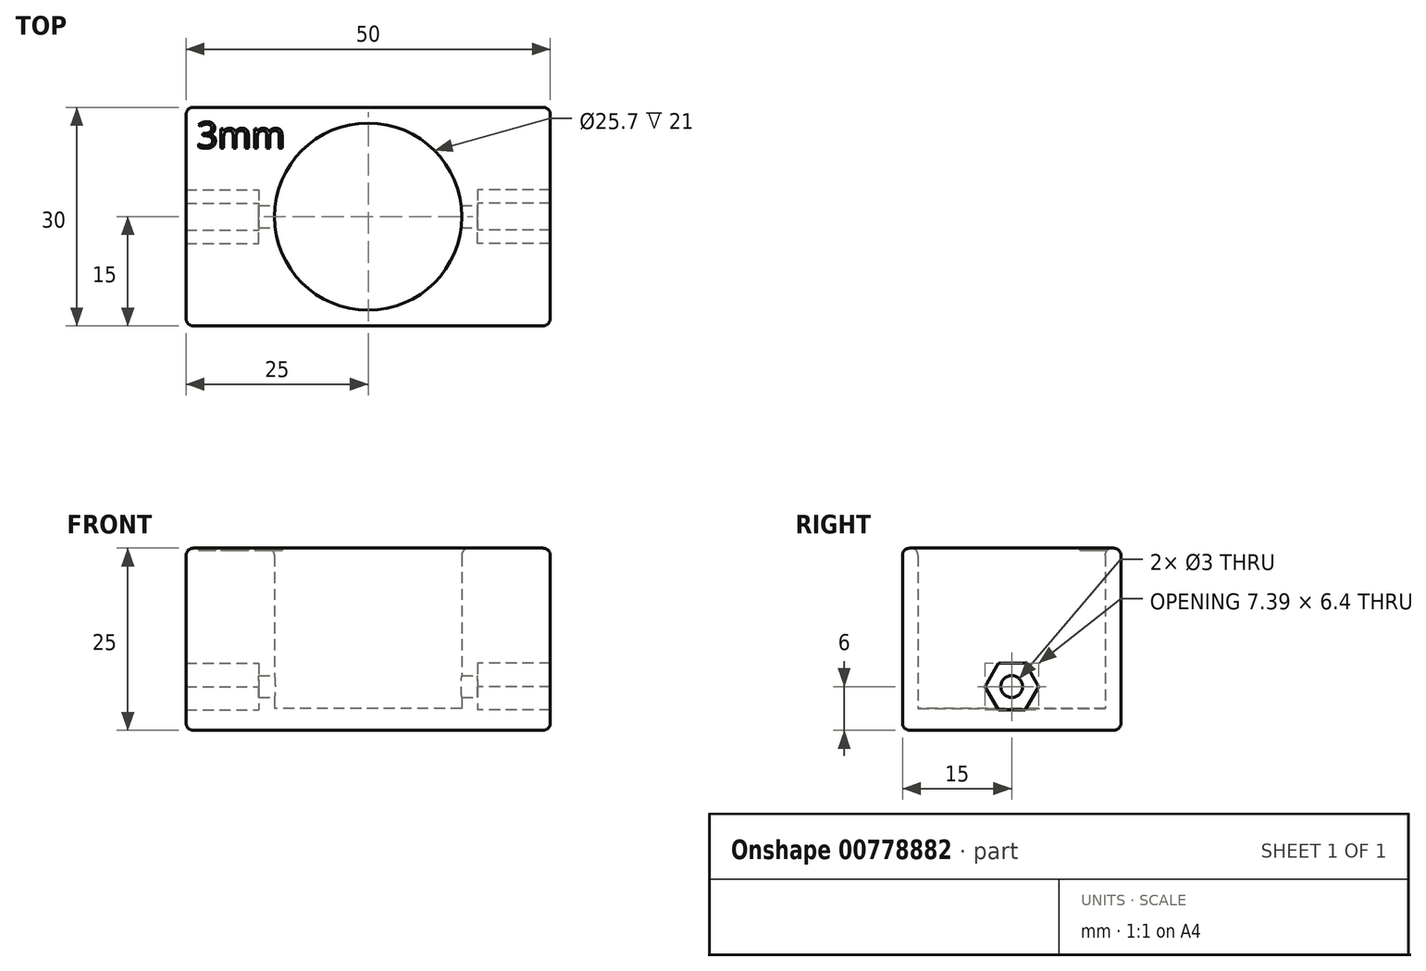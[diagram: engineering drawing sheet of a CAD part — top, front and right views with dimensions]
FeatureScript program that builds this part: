
annotation { "Feature Type Name" : "Feature", "Feature Type Description" : "" }
export const myFeature = defineFeature(function(context is Context, id is Id, definition is map)
    precondition{}
    {
        {
            var Q0;
            Q0=qCreatedBy(makeId("Top.planeOp"),FACE);
            var sketch = newSketch(context, id + "F0", { "sketchPlane" : qUnion([Q0])});
            skCircle(sketch, "E0", {"center": v(0, 0) * mm, "radius": 12.85 * mm});
            skLineSegment(sketch, "E1.bottom", {"start": v(25, -15) * mm, "end": v(-25, -15) * mm});
            skLineSegment(sketch, "E1.top", {"start": v(25, 15) * mm, "end": v(-25, 15) * mm});
            skLineSegment(sketch, "E1.left", {"start": v(25, -15) * mm, "end": v(25, 15) * mm});
            skLineSegment(sketch, "E1.right", {"start": v(-25, -15) * mm, "end": v(-25, 15) * mm});
            skSolve(sketch);
        }
        {
            var Q0;
            Q0=makeQuery(id+"F0.imprint","IMPRINT",FACE,{"disambiguationData":[TD([[makeQuery(id+"F0.imprint","IMPRINT",EDGE,{"derivedFrom":sQuery(id+"F0.wireOp",EDGE,"E0")}),1.0]])]});
            extrude(context, id + "F1", {"entities" : qUnion([Q0]), "depth" : 3 * mm, "offsetDistance" : 25 * mm});
        }
        {
            var Q0;
            Q0=makeQuery(id+"F0.imprint","IMPRINT",FACE,{"disambiguationData":[TD([[makeQuery(id+"F0.imprint","IMPRINT",EDGE,{"derivedFrom":sQuery(id+"F0.wireOp",EDGE,"E0")}),-1.0]])]});
            extrude(context, id + "F2", {"entities" : qUnion([Q0]), "operationType" : NewBodyOperationType.ADD, "depth" : 25 * mm, "offsetDistance" : 25 * mm});
        }
        {
            var Q0;
            Q0=makeQuery(id+"F2.opExtrude","SWEPT_EDGE",EDGE,{"disambiguationData":[OSD([sQuery(id+"F0.wireOp",EDGE,"E1.top"),sQuery(id+"F0.wireOp",EDGE,"E1.right")])]});
            var Q1;
            Q1=makeQuery(id+"F2.opExtrude","SWEPT_EDGE",EDGE,{"disambiguationData":[OSD([sQuery(id+"F0.wireOp",EDGE,"E1.top"),sQuery(id+"F0.wireOp",EDGE,"E1.left")])]});
            var Q2;
            Q2=makeQuery(id+"F2.opExtrude","SWEPT_EDGE",EDGE,{"disambiguationData":[OSD([sQuery(id+"F0.wireOp",EDGE,"E1.bottom"),sQuery(id+"F0.wireOp",EDGE,"E1.right")])]});
            var Q3;
            Q3=makeQuery(id+"F2.opExtrude","SWEPT_EDGE",EDGE,{"disambiguationData":[OSD([sQuery(id+"F0.wireOp",EDGE,"E1.bottom"),sQuery(id+"F0.wireOp",EDGE,"E1.left")])]});
            var Q4;
            Q4=makeQuery(id+"F2.opExtrude","CAP_EDGE",EDGE,{"disambiguationData":[OSD([sQuery(id+"F0.wireOp",EDGE,"E1.left")])],"isStart":true});
            var Q5;
            Q5=makeQuery(id+"F2.opExtrude","CAP_EDGE",EDGE,{"disambiguationData":[OSD([sQuery(id+"F0.wireOp",EDGE,"E1.top")])],"isStart":true});
            var Q6;
            Q6=makeQuery(id+"F2.opExtrude","CAP_EDGE",EDGE,{"disambiguationData":[OSD([sQuery(id+"F0.wireOp",EDGE,"E1.right")])],"isStart":true});
            var Q7;
            Q7=makeQuery(id+"F2.opExtrude","CAP_EDGE",EDGE,{"disambiguationData":[OSD([sQuery(id+"F0.wireOp",EDGE,"E1.bottom")])],"isStart":true});
            var Q8;
            Q8=makeQuery(id+"F2.opExtrude","CAP_EDGE",EDGE,{"disambiguationData":[OSD([sQuery(id+"F0.wireOp",EDGE,"E1.bottom")])],"isStart":false});
            var Q9;
            Q9=makeQuery(id+"F2.opExtrude","CAP_EDGE",EDGE,{"disambiguationData":[OSD([sQuery(id+"F0.wireOp",EDGE,"E1.top")])],"isStart":false});
            var Q10;
            Q10=makeQuery(id+"F2.opExtrude","CAP_EDGE",EDGE,{"disambiguationData":[OSD([sQuery(id+"F0.wireOp",EDGE,"E1.right")])],"isStart":false});
            var Q11;
            Q11=makeQuery(id+"F2.opExtrude","CAP_EDGE",EDGE,{"disambiguationData":[OSD([sQuery(id+"F0.wireOp",EDGE,"E1.left")])],"isStart":false});
            var Q12;
            Q12=makeQuery(id+"F2.opExtrude","CAP_EDGE",EDGE,{"disambiguationData":[OSD([sQuery(id+"F0.wireOp",EDGE,"E0")])],"isStart":false});
            fillet(context, id + "F3", {"entities" : qUnion([Q0, Q1, Q2, Q3, Q4, Q5, Q6, Q7, Q8, Q9, Q10, Q11, Q12]), "radius" : 1 * mm, "tangentPropagation" : true, "allowEdgeOverflow" : false});
        }
        {
            var Q0;
            Q0=qCreatedBy(makeId("Right.planeOp"),FACE);
            var sketch = newSketch(context, id + "F4", { "sketchPlane" : qUnion([Q0])});
            skLineSegment(sketch, "E2", {"start": v(0, 0) * mm, "end": v(0, 6) * mm});
            skCircle(sketch, "E3.cCircle", {"center": v(0, 6) * mm, "radius": 3.2 * mm, "construction": true});
            skLineSegment(sketch, "E3.0", {"start": v(1.85, 2.8) * mm, "end": v(-1.85, 2.8) * mm});
            skLineSegment(sketch, "E3.1", {"start": v(-1.85, 2.8) * mm, "end": v(-3.7, 6) * mm});
            skLineSegment(sketch, "E3.2", {"start": v(-3.7, 6) * mm, "end": v(-1.85, 9.2) * mm});
            skLineSegment(sketch, "E3.3", {"start": v(-1.85, 9.2) * mm, "end": v(1.85, 9.2) * mm});
            skLineSegment(sketch, "E3.4", {"start": v(1.85, 9.2) * mm, "end": v(3.7, 6) * mm});
            skLineSegment(sketch, "E3.5", {"start": v(3.7, 6) * mm, "end": v(1.85, 2.8) * mm});
            skPoint(sketch, "E3.0.midPoint", {"position": v(0, 2.8) * mm});
            skSolve(sketch);
        }
        {
            var Q0;
            Q0 = qSketchRegion(id + "F4", true);
            extrude(context, id + "F5", {"entities" : qUnion([Q0]), "operationType" : NewBodyOperationType.REMOVE, "oppositeDirection" : true, "depth" : 40 * mm, "offsetDistance" : 25 * mm, "hasSecondDirection" : true, "secondDirectionOppositeDirection" : true, "secondDirectionDepth" : 15 * mm});
        }
        {
            var Q0;
            {var subQ0=sQuery(id+"F4.wireOp",EDGE,"E3.1");Q0=makeQuery(id+"F4.imprint","IMPRINT",FACE,{"disambiguationData":[TD([[makeQuery(id+"F4.imprint","IMPRINT",EDGE,{"derivedFrom":subQ0}),-1.0]])]});}
            extrude(context, id + "F6", {"entities" : qUnion([Q0]), "operationType" : NewBodyOperationType.REMOVE, "depth" : 40 * mm, "offsetDistance" : 25 * mm, "hasSecondDirection" : true, "secondDirectionOppositeDirection" : false, "secondDirectionDepth" : 15 * mm});
        }
        {
            var Q0;
            Q0=qCreatedBy(makeId("Right.planeOp"),FACE);
            var sketch = newSketch(context, id + "F7", { "sketchPlane" : qUnion([Q0])});
            skLineSegment(sketch, "E4", {"start": v(0, 0) * mm, "end": v(0, 6) * mm, "construction": true});
            skCircle(sketch, "E5", {"center": v(0, 6) * mm, "radius": 1.5 * mm});
            skSolve(sketch);
        }
        {
            var Q0;
            Q0 = qSketchRegion(id + "F7", true);
            extrude(context, id + "F8", {"entities" : qUnion([Q0]), "operationType" : NewBodyOperationType.REMOVE, "oppositeDirection" : true, "depth" : 50 * mm, "offsetDistance" : 25 * mm, "hasSecondDirection" : true, "secondDirectionOppositeDirection" : false, "secondDirectionDepth" : 50 * mm});
        }
        {
            var Q0;
            Q0=qCreatedBy(makeId("Top.planeOp"),FACE);
            var sketch = newSketch(context, id + "F9", { "sketchPlane" : qUnion([Q0])});
            skText(sketch, "E6", { "text": "3mm", "fontName": "OpenSans-Regular.ttf"});
            const initialGuessF9  = {"E6": [-0.0235, 0.00942, 1, 0, 0.00358]};
            skSetInitialGuess(sketch, initialGuessF9);
            skSolve(sketch);
        }
        {
            var Q0;
            Q0 = qSketchRegion(id + "F9", true);
            extrude(context, id + "F10", {"entities" : qUnion([Q0]), "operationType" : NewBodyOperationType.REMOVE, "depth" : 30 * mm, "offsetDistance" : 25 * mm, "hasSecondDirection" : true, "secondDirectionOppositeDirection" : false, "secondDirectionDepth" : 24.7 * mm});
        }
    });
